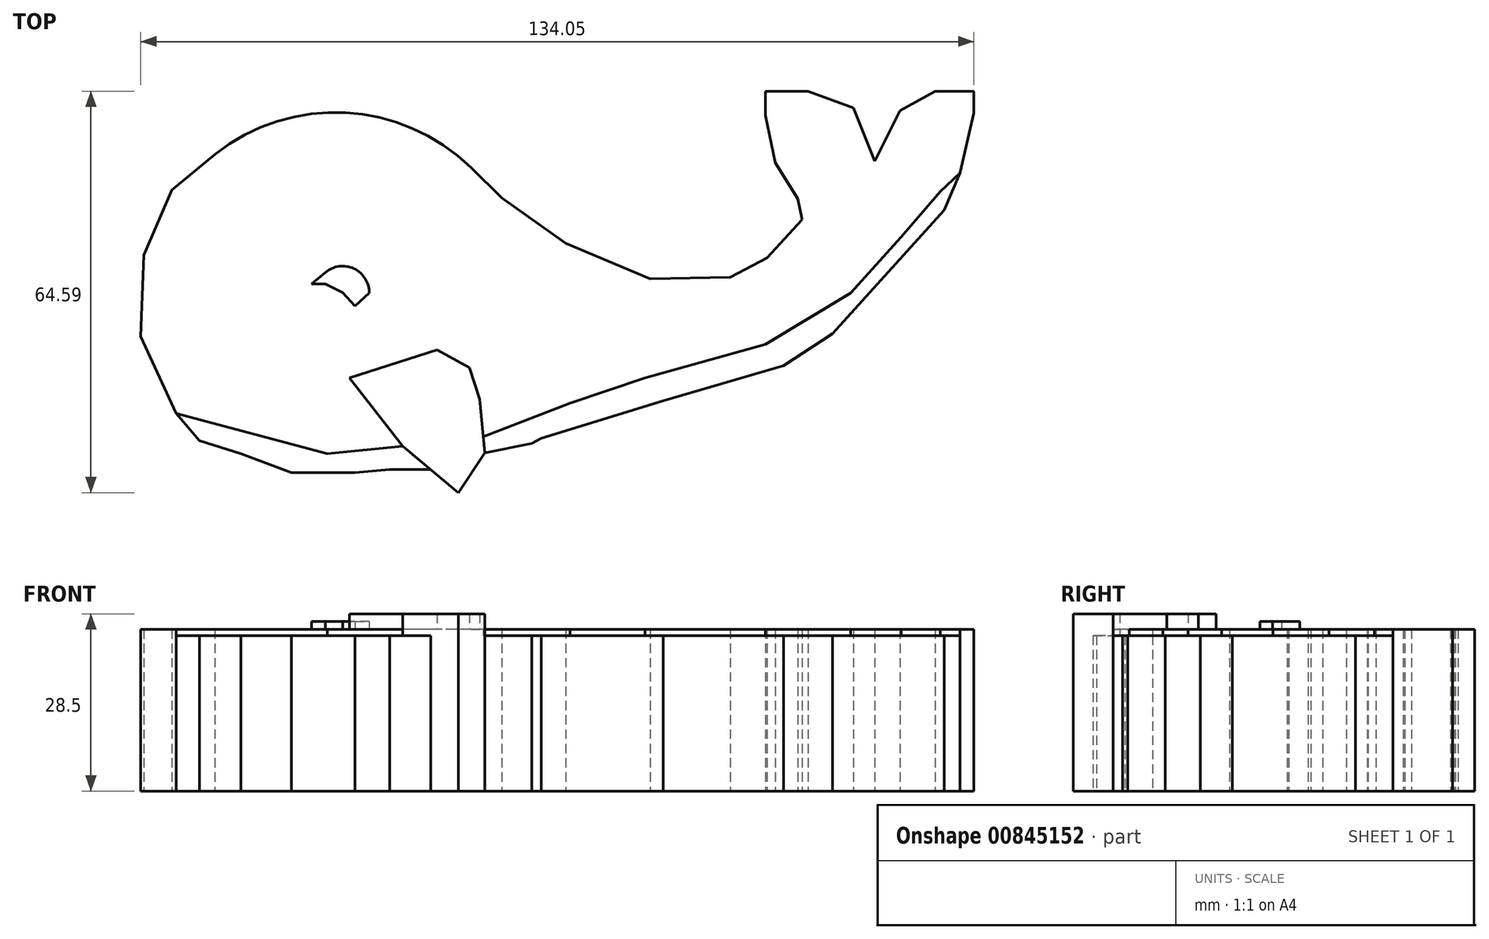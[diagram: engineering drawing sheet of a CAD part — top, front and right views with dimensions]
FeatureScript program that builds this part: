
annotation { "Feature Type Name" : "Feature", "Feature Type Description" : "" }
export const myFeature = defineFeature(function(context is Context, id is Id, definition is map)
    precondition{}
    {
        {
            var Q0;
            Q0=qCreatedBy(makeId("Top.planeOp"),FACE);
            var sketch = newSketch(context, id + "F0", { "sketchPlane" : qUnion([Q0])});
            skArc(sketch, "E0", {"start": v(-9.77, 33.84) * mm, "mid": v(-29.98, 42.7) * mm, "end": v(-51, 35.98) * mm});
            skLineSegment(sketch, "E1", {"start": v(-9.77, 33.84) * mm, "end": v(-4.83, 29) * mm});
            skLineSegment(sketch, "E2", {"start": v(-4.83, 29) * mm, "end": v(5.48, 21.68) * mm});
            skLineSegment(sketch, "E3", {"start": v(5.48, 21.68) * mm, "end": v(19.06, 15.96) * mm});
            skLineSegment(sketch, "E4", {"start": v(18.23, 0) * mm, "end": v(6.2, -4.05) * mm});
            skLineSegment(sketch, "E5", {"start": v(6.2, -4.05) * mm, "end": v(-8.58, -9.77) * mm});
            skLineSegment(sketch, "E6", {"start": v(-8.58, -9.77) * mm, "end": v(-32.88, -12.15) * mm});
            skLineSegment(sketch, "E7", {"start": v(-32.88, -12.15) * mm, "end": v(-57.19, -5.72) * mm});
            skLineSegment(sketch, "E8", {"start": v(-57.19, -5.72) * mm, "end": v(-62.9, 6.67) * mm});
            skLineSegment(sketch, "E9", {"start": v(-62.9, 6.67) * mm, "end": v(-62.43, 19.78) * mm});
            skLineSegment(sketch, "E10", {"start": v(-62.43, 19.78) * mm, "end": v(-57.9, 30.26) * mm});
            skLineSegment(sketch, "E11", {"start": v(-57.9, 30.26) * mm, "end": v(-51, 35.98) * mm});
            skLineSegment(sketch, "E12", {"start": v(-29.3, 0) * mm, "end": v(-20.73, -10.96) * mm});
            skLineSegment(sketch, "E13", {"start": v(-20.73, -10.96) * mm, "end": v(-11.77, -18.44) * mm});
            skLineSegment(sketch, "E14", {"start": v(-11.77, -18.44) * mm, "end": v(-7.53, -12.06) * mm});
            skLineSegment(sketch, "E15", {"start": v(-7.53, -12.06) * mm, "end": v(-8.38, -3.42) * mm});
            skLineSegment(sketch, "E16", {"start": v(-8.38, -3.42) * mm, "end": v(-10, 1.67) * mm});
            skLineSegment(sketch, "E17", {"start": v(-10, 1.67) * mm, "end": v(-15.25, 4.53) * mm});
            skLineSegment(sketch, "E18", {"start": v(-15.25, 4.53) * mm, "end": v(-29.3, 0) * mm});
            skLineSegment(sketch, "E19", {"start": v(-15.25, 4.53) * mm, "end": v(-10, 1.67) * mm});
            skPoint(sketch, "E20.end.orphan", {"position": v(34.07, 1.43) * mm});
            skPoint(sketch, "E21.end.orphan", {"position": v(34.07, 13.34) * mm});
            skLineSegment(sketch, "E22", {"start": v(18.23, 0) * mm, "end": v(37.64, 5.41) * mm});
            skLineSegment(sketch, "E23", {"start": v(37.64, 5.41) * mm, "end": v(51.3, 13.66) * mm});
            skLineSegment(sketch, "E24", {"start": v(51.3, 13.66) * mm, "end": v(59.48, 22.68) * mm});
            skLineSegment(sketch, "E25", {"start": v(59.48, 22.68) * mm, "end": v(65.74, 29.98) * mm});
            skLineSegment(sketch, "E26", {"start": v(65.74, 29.98) * mm, "end": v(68.9, 32.97) * mm});
            skLineSegment(sketch, "E27", {"start": v(55.19, 34.9) * mm, "end": v(51.77, 43.44) * mm});
            skLineSegment(sketch, "E28", {"start": v(51.77, 43.44) * mm, "end": v(44.48, 46.15) * mm});
            skLineSegment(sketch, "E29", {"start": v(44.48, 46.15) * mm, "end": v(37.64, 46.15) * mm});
            skLineSegment(sketch, "E30", {"start": v(37.64, 46.15) * mm, "end": v(37.64, 42.27) * mm});
            skLineSegment(sketch, "E31", {"start": v(37.64, 42.27) * mm, "end": v(39.2, 34.63) * mm});
            skLineSegment(sketch, "E32", {"start": v(37.9, 19.33) * mm, "end": v(31.96, 16.24) * mm});
            skLineSegment(sketch, "E33", {"start": v(31.96, 16.24) * mm, "end": v(19.06, 15.96) * mm});
            skPoint(sketch, "E34.start.orphan", {"position": v(59.48, 45.1) * mm});
            skLineSegment(sketch, "E35", {"start": v(55.19, 34.9) * mm, "end": v(59.27, 43.02) * mm});
            skLineSegment(sketch, "E36", {"start": v(59.27, 43.02) * mm, "end": v(64.9, 46.15) * mm});
            skLineSegment(sketch, "E37", {"start": v(64.9, 46.15) * mm, "end": v(71.15, 46.15) * mm});
            skLineSegment(sketch, "E38", {"start": v(71.15, 46.15) * mm, "end": v(71.15, 42.6) * mm});
            skLineSegment(sketch, "E39", {"start": v(71.15, 42.6) * mm, "end": v(68.9, 32.97) * mm});
            skLineSegment(sketch, "E40", {"start": v(68.9, 32.97) * mm, "end": v(66.37, 26.98) * mm});
            skLineSegment(sketch, "E41", {"start": v(66.37, 26.98) * mm, "end": v(48.33, 7.1) * mm});
            skLineSegment(sketch, "E42", {"start": v(48.44, 7.19) * mm, "end": v(48.33, 7.1) * mm});
            skLineSegment(sketch, "E43", {"start": v(48.44, 7.19) * mm, "end": v(40.52, 1.98) * mm});
            skLineSegment(sketch, "E44", {"start": v(21.15, -3.65) * mm, "end": v(1.51, -9.68) * mm});
            skLineSegment(sketch, "E45", {"start": v(1.51, -9.68) * mm, "end": v(0, -10.52) * mm});
            skLineSegment(sketch, "E46", {"start": v(0, -10.52) * mm, "end": v(-7.53, -12.06) * mm});
            skLineSegment(sketch, "E47", {"start": v(-22.82, -14.7) * mm, "end": v(-28.44, -15.25) * mm});
            skPoint(sketch, "E47.startSnap0", {"position": v(-16.25, -14.7) * mm});
            skPoint(sketch, "E47.endSnap0", {"position": v(-9.65, -15.25) * mm});
            skLineSegment(sketch, "E48", {"start": v(-28.44, -15.25) * mm, "end": v(-38.65, -15.25) * mm});
            skLineSegment(sketch, "E49", {"start": v(-38.65, -15.25) * mm, "end": v(-46.77, -12.19) * mm});
            skLineSegment(sketch, "E50", {"start": v(-46.77, -12.19) * mm, "end": v(-53.44, -10.1) * mm});
            skLineSegment(sketch, "E51", {"start": v(-53.44, -10.1) * mm, "end": v(-57.19, -5.72) * mm});
            skLineSegment(sketch, "E52", {"start": v(-22.82, -14.7) * mm, "end": v(-16.25, -14.7) * mm});
            skLineSegment(sketch, "E53", {"start": v(40.52, 1.98) * mm, "end": v(21.15, -3.65) * mm});
            skPoint(sketch, "E54.endSnap0", {"position": v(41.08, 21) * mm});
            skPoint(sketch, "E55.orphan", {"position": v(44.26, 22.68) * mm});
            skLineSegment(sketch, "E56", {"start": v(39.2, 34.63) * mm, "end": v(42.81, 28.85) * mm});
            skLineSegment(sketch, "E57", {"start": v(42.81, 28.85) * mm, "end": v(43.5, 25.5) * mm});
            skLineSegment(sketch, "E58", {"start": v(43.5, 25.5) * mm, "end": v(37.9, 19.33) * mm});
            skPoint(sketch, "E59.start.orphan", {"position": v(41.08, 25.94) * mm});
            skPoint(sketch, "E60.end.orphan", {"position": v(-21.55, 11.5) * mm});
            skPoint(sketch, "E61.start.orphan", {"position": v(-40.3, 16.24) * mm});
            skArc(sketch, "E62", {"start": v(-26.13, 13.65) * mm, "mid": v(-28.6, 17.6) * mm, "end": v(-33.21, 16.98) * mm});
            skLineSegment(sketch, "E63", {"start": v(-33.21, 16.98) * mm, "end": v(-35.42, 15.1) * mm});
            skLineSegment(sketch, "E64", {"start": v(-35.42, 15.1) * mm, "end": v(-33.21, 15.1) * mm});
            skLineSegment(sketch, "E65", {"start": v(-33.21, 15.1) * mm, "end": v(-30.43, 13.7) * mm});
            skLineSegment(sketch, "E66", {"start": v(-30.43, 13.7) * mm, "end": v(-28.42, 11.56) * mm});
            skLineSegment(sketch, "E67", {"start": v(-28.42, 11.56) * mm, "end": v(-26.13, 13.65) * mm});
            skPoint(sketch, "E68", {"position": v(67.63, 29.98) * mm});
            skSolve(sketch);
        }
        {
            var Q0;
            {var subQ4=sQuery(id+"F0.wireOp",EDGE,"E12");Q0=makeQuery(id+"F0.imprint","IMPRINT",FACE,{"disambiguationData":[TD([[makeQuery(id+"F0.imprint","IMPRINT",EDGE,{"derivedFrom":subQ4}),1.0]])]});}
            var Q1;
            {var subQ7=sQuery(id+"F0.wireOp",EDGE,"E14");Q1=makeQuery(id+"F0.imprint","IMPRINT",FACE,{"disambiguationData":[TD([[makeQuery(id+"F0.imprint","IMPRINT",EDGE,{"derivedFrom":subQ7}),1.0]])]});}
            extrude(context, id + "F1", {"entities" : qUnion([Q0, Q1]), "depth" : 28.5 * mm, "offsetDistance" : 25 * mm});
        }
        {
            var Q0;
            {var subQ4=sQuery(id+"F0.wireOp",EDGE,"E7");Q0=makeQuery(id+"F0.imprint","IMPRINT",FACE,{"disambiguationData":[TD([[makeQuery(id+"F0.imprint","IMPRINT",EDGE,{"derivedFrom":subQ4}),1.0]])]});}
            extrude(context, id + "F2", {"entities" : qUnion([Q0]), "operationType" : NewBodyOperationType.ADD, "depth" : 25 * mm, "offsetDistance" : 25 * mm});
        }
        {
            var Q0;
            {var subQ4=sQuery(id+"F0.wireOp",EDGE,"E4");Q0=makeQuery(id+"F0.imprint","IMPRINT",FACE,{"disambiguationData":[TD([[makeQuery(id+"F0.imprint","IMPRINT",EDGE,{"derivedFrom":subQ4}),1.0]])]});}
            extrude(context, id + "F3", {"entities" : qUnion([Q0]), "operationType" : NewBodyOperationType.ADD, "depth" : 25 * mm, "offsetDistance" : 25 * mm});
        }
        {
            var Q0;
            Q0=makeQuery(id+"F0.imprint","IMPRINT",FACE,{"disambiguationData":[TD([[makeQuery(id+"F0.imprint","IMPRINT",EDGE,{"derivedFrom":sQuery(id+"F0.wireOp",EDGE,"E0")}),1.0]])]});
            extrude(context, id + "F4", {"entities" : qUnion([Q0]), "operationType" : NewBodyOperationType.ADD, "depth" : 26 * mm, "offsetDistance" : 25 * mm});
        }
        {
            var Q0;
            Q0=makeQuery(id+"F0.imprint","IMPRINT",FACE,{"disambiguationData":[TD([[makeQuery(id+"F0.imprint","IMPRINT",EDGE,{"derivedFrom":sQuery(id+"F0.wireOp",EDGE,"E62")}),1.0]])]});
            extrude(context, id + "F5", {"entities" : qUnion([Q0]), "operationType" : NewBodyOperationType.ADD, "depth" : 27.3 * mm, "offsetDistance" : 25 * mm});
        }
    });
